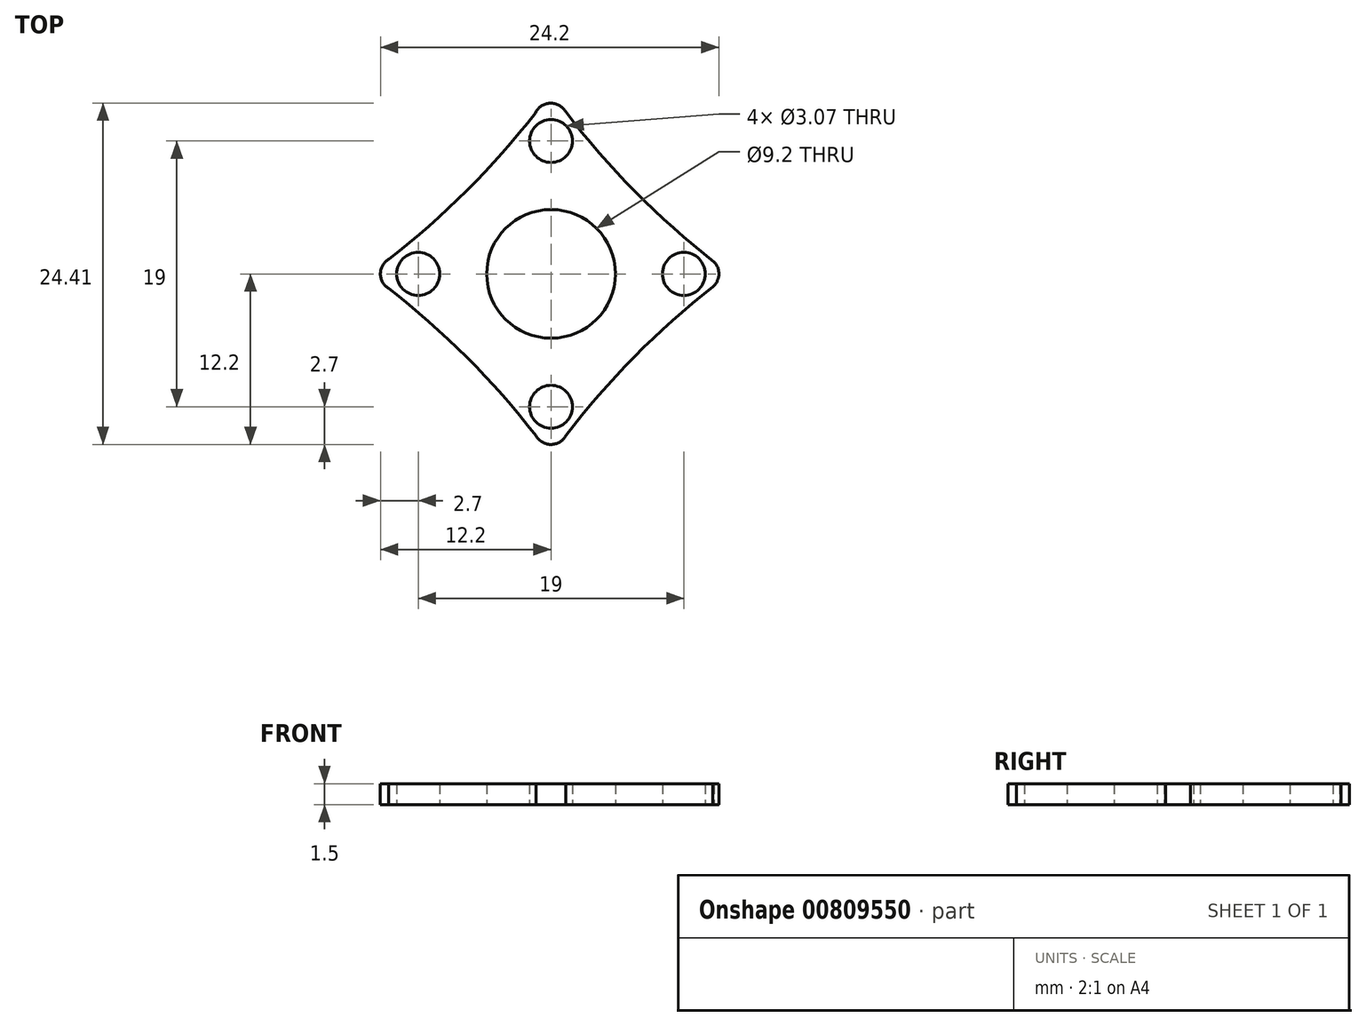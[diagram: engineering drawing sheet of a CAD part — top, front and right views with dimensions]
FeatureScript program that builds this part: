
annotation { "Feature Type Name" : "Feature", "Feature Type Description" : "" }
export const myFeature = defineFeature(function(context is Context, id is Id, definition is map)
    precondition{}
    {
        {
            var Q0;
            Q0=qCreatedBy(makeId("Top.planeOp"),FACE);
            var sketch = newSketch(context, id + "F0", { "sketchPlane" : qUnion([Q0])});
            skLineSegment(sketch, "E0", {"start": v(-9.5, 0) * mm, "end": v(9.5, 0) * mm});
            skLineSegment(sketch, "E1", {"start": v(0, 9.5) * mm, "end": v(0, -9.5) * mm});
            skCircle(sketch, "E2", {"center": v(0, 0) * mm, "radius": 4.6 * mm});
            skCircle(sketch, "E3", {"center": v(-9.5, 0) * mm, "radius": 1.53 * mm});
            skCircle(sketch, "E4", {"center": v(9.5, 0) * mm, "radius": 1.53 * mm});
            skCircle(sketch, "E5", {"center": v(0, 9.5) * mm, "radius": 1.53 * mm});
            skCircle(sketch, "E6", {"center": v(0, -9.5) * mm, "radius": 1.53 * mm});
            skLineSegment(sketch, "E7", {"start": v(0, -13) * mm, "end": v(0, -9.5) * mm});
            skLineSegment(sketch, "E8", {"start": v(12.78, 0) * mm, "end": v(9.28, 0) * mm});
            skLineSegment(sketch, "E9", {"start": v(-9.5, 0) * mm, "end": v(-13, 0) * mm});
            skLineSegment(sketch, "E10", {"start": v(0, 9.5) * mm, "end": v(0, 13) * mm});
            skArc(sketch, "E11", {"start": v(-13, 0) * mm, "mid": v(-6, 6) * mm, "end": v(0, 13) * mm});
            skArc(sketch, "E12", {"start": v(0, 13) * mm, "mid": v(5.89, 6) * mm, "end": v(12.78, 0) * mm});
            skArc(sketch, "E13", {"start": v(12.78, 0) * mm, "mid": v(5.89, -6) * mm, "end": v(0, -13) * mm});
            skArc(sketch, "E14", {"start": v(0, -13) * mm, "mid": v(-6, -6) * mm, "end": v(-13, 0) * mm});
            skArc(sketch, "E15", {"start": v(-1.08, -11.56) * mm, "mid": v(-0.02, -12.2) * mm, "end": v(1.05, -11.58) * mm});
            skArc(sketch, "E16", {"start": v(-11.58, 1.06) * mm, "mid": v(-12.2, 0.03) * mm, "end": v(-11.62, -1.04) * mm});
            skArc(sketch, "E17", {"start": v(11.55, -0.94) * mm, "mid": v(12, 0.1) * mm, "end": v(11.4, 1.07) * mm});
            skArc(sketch, "E18", {"start": v(1.04, 11.6) * mm, "mid": v(-0.06, 12.2) * mm, "end": v(-1.11, 11.52) * mm});
            skSolve(sketch);
        }
        {
            var Q0;
            {var subQ0=sQuery(id+"F0.wireOp",EDGE,"E16");var subQ1=sQuery(id+"F0.wireOp",EDGE,"E11");var subQ2=makeQuery(id+"F0.imprint","INTERSECT",VERTEX,{"disambiguationData":[OD(0.0)],"derivedFrom":[subQ1,subQ0]});Q0=makeQuery(id+"F0.imprint","IMPRINT",FACE,{"disambiguationData":[TD([[makeQuery(id+"F0.imprint","IMPRINT",EDGE,{"disambiguationData":[TD([[subQ2,1.0]])],"derivedFrom":subQ1}),1.0]])]});}
            var Q1;
            {var subQ0=sQuery(id+"F0.wireOp",EDGE,"E18");var subQ1=sQuery(id+"F0.wireOp",EDGE,"E11");var subQ2=makeQuery(id+"F0.imprint","INTERSECT",VERTEX,{"disambiguationData":[OD(0.0)],"derivedFrom":[subQ1,subQ0]});Q1=makeQuery(id+"F0.imprint","IMPRINT",FACE,{"disambiguationData":[TD([[makeQuery(id+"F0.imprint","IMPRINT",EDGE,{"disambiguationData":[TD([[subQ2,-1.0]])],"derivedFrom":subQ1}),1.0]])]});}
            var Q2;
            {var subQ0=sQuery(id+"F0.wireOp",EDGE,"E18");var subQ1=sQuery(id+"F0.wireOp",EDGE,"E12");var subQ2=makeQuery(id+"F0.imprint","INTERSECT",VERTEX,{"disambiguationData":[OD(0.0)],"derivedFrom":[subQ1,subQ0]});Q2=makeQuery(id+"F0.imprint","IMPRINT",FACE,{"disambiguationData":[TD([[makeQuery(id+"F0.imprint","IMPRINT",EDGE,{"disambiguationData":[TD([[subQ2,1.0]])],"derivedFrom":subQ1}),1.0]])]});}
            var Q3;
            {var subQ0=sQuery(id+"F0.wireOp",EDGE,"E17");var subQ1=sQuery(id+"F0.wireOp",EDGE,"E12");var subQ2=makeQuery(id+"F0.imprint","INTERSECT",VERTEX,{"disambiguationData":[OD(0.0)],"derivedFrom":[subQ1,subQ0]});Q3=makeQuery(id+"F0.imprint","IMPRINT",FACE,{"disambiguationData":[TD([[makeQuery(id+"F0.imprint","IMPRINT",EDGE,{"disambiguationData":[TD([[subQ2,-1.0]])],"derivedFrom":subQ1}),1.0]])]});}
            var Q4;
            {var subQ0=sQuery(id+"F0.wireOp",EDGE,"E15");var subQ1=sQuery(id+"F0.wireOp",EDGE,"E13");var subQ2=makeQuery(id+"F0.imprint","INTERSECT",VERTEX,{"disambiguationData":[OD(0.0)],"derivedFrom":[subQ1,subQ0]});Q4=makeQuery(id+"F0.imprint","IMPRINT",FACE,{"disambiguationData":[TD([[makeQuery(id+"F0.imprint","IMPRINT",EDGE,{"disambiguationData":[TD([[subQ2,-1.0]])],"derivedFrom":subQ1}),1.0]])]});}
            var Q5;
            {var subQ0=sQuery(id+"F0.wireOp",EDGE,"E15");var subQ1=sQuery(id+"F0.wireOp",EDGE,"E14");var subQ2=makeQuery(id+"F0.imprint","INTERSECT",VERTEX,{"disambiguationData":[OD(0.0)],"derivedFrom":[subQ1,subQ0]});Q5=makeQuery(id+"F0.imprint","IMPRINT",FACE,{"disambiguationData":[TD([[makeQuery(id+"F0.imprint","IMPRINT",EDGE,{"disambiguationData":[TD([[subQ2,1.0]])],"derivedFrom":subQ1}),1.0]])]});}
            var Q6;
            {var subQ0=sQuery(id+"F0.wireOp",EDGE,"E16");var subQ1=sQuery(id+"F0.wireOp",EDGE,"E14");var subQ2=makeQuery(id+"F0.imprint","INTERSECT",VERTEX,{"disambiguationData":[OD(0.0)],"derivedFrom":[subQ1,subQ0]});Q6=makeQuery(id+"F0.imprint","IMPRINT",FACE,{"disambiguationData":[TD([[makeQuery(id+"F0.imprint","IMPRINT",EDGE,{"disambiguationData":[TD([[subQ2,-1.0]])],"derivedFrom":subQ1}),1.0]])]});}
            var Q7;
            {var subQ16=sQuery(id+"F0.wireOp",EDGE,"E0");var subQ18=sQuery(id+"F0.wireOp",EDGE,"E2");var subQ20=makeQuery(id+"F0.imprint","INTERSECT",VERTEX,{"disambiguationData":[OD(1.0)],"derivedFrom":[subQ16,subQ18]});Q7=makeQuery(id+"F0.imprint","IMPRINT",FACE,{"disambiguationData":[TD([[makeQuery(id+"F0.imprint","IMPRINT",EDGE,{"disambiguationData":[TD([[subQ20,-1.0]])],"derivedFrom":subQ16}),-1.0]])]});}
            var Q8;
            {var subQ5=sQuery(id+"F0.wireOp",EDGE,"E3");var subQ6=sQuery(id+"F0.wireOp",EDGE,"E0");var subQ7=makeQuery(id+"F0.imprint","INTERSECT",VERTEX,{"derivedFrom":[subQ6,subQ5]});Q8=makeQuery(id+"F0.imprint","IMPRINT",FACE,{"disambiguationData":[TD([[makeQuery(id+"F0.imprint","IMPRINT",EDGE,{"disambiguationData":[TD([[subQ7,-1.0]])],"derivedFrom":subQ6}),1.0]])]});}
            var Q9;
            {var subQ11=sQuery(id+"F0.wireOp",EDGE,"E3");var subQ12=sQuery(id+"F0.wireOp",EDGE,"E0");var subQ13=makeQuery(id+"F0.imprint","INTERSECT",VERTEX,{"derivedFrom":[subQ12,subQ11]});Q9=makeQuery(id+"F0.imprint","IMPRINT",FACE,{"disambiguationData":[TD([[makeQuery(id+"F0.imprint","IMPRINT",EDGE,{"disambiguationData":[TD([[subQ13,-1.0]])],"derivedFrom":subQ12}),-1.0]])]});}
            var Q10;
            {var subQ11=sQuery(id+"F0.wireOp",EDGE,"E2");var subQ12=sQuery(id+"F0.wireOp",EDGE,"E0");var subQ13=makeQuery(id+"F0.imprint","INTERSECT",VERTEX,{"disambiguationData":[OD(1.0)],"derivedFrom":[subQ12,subQ11]});Q10=makeQuery(id+"F0.imprint","IMPRINT",FACE,{"disambiguationData":[TD([[makeQuery(id+"F0.imprint","IMPRINT",EDGE,{"disambiguationData":[TD([[subQ13,-1.0]])],"derivedFrom":subQ12}),1.0]])]});}
            extrude(context, id + "F1", {"entities" : qUnion([Q0, Q1, Q2, Q3, Q4, Q5, Q6, Q7, Q8, Q9, Q10]), "depth" : 1.5 * mm, "offsetDistance" : 25 * mm});
        }
    });
